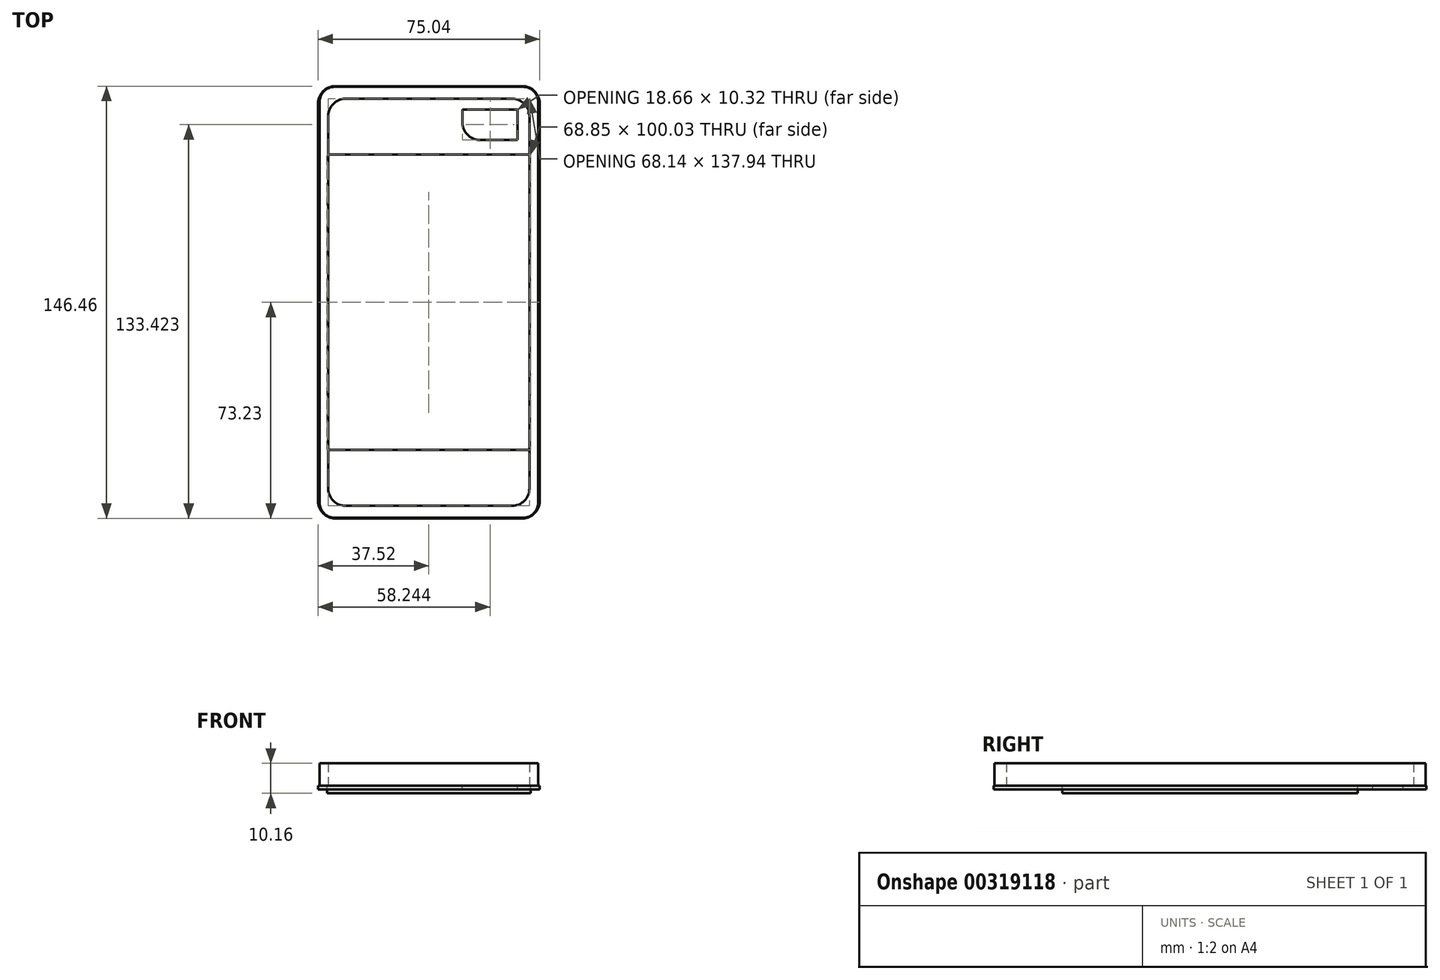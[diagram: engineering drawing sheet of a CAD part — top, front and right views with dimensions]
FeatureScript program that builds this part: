
annotation { "Feature Type Name" : "Feature", "Feature Type Description" : "" }
export const myFeature = defineFeature(function(context is Context, id is Id, definition is map)
    precondition{}
    {
        {
            var Q0;
            Q0=qCreatedBy(makeId("Top.planeOp"),FACE);
            var sketch = newSketch(context, id + "F0", { "sketchPlane" : qUnion([Q0])});
            skLineSegment(sketch, "E0.bottom", {"start": v(-31.96, 72.99) * mm, "end": v(31.96, 72.99) * mm});
            skLineSegment(sketch, "E0.top", {"start": v(-31.96, -72.99) * mm, "end": v(31.96, -72.99) * mm});
            skLineSegment(sketch, "E0.left", {"start": v(-37.04, 67.9) * mm, "end": v(-37.04, -67.9) * mm});
            skLineSegment(sketch, "E0.right", {"start": v(37.04, 67.9) * mm, "end": v(37.04, -67.9) * mm});
            skPoint(sketch, "E0.middle", {"position": v(0, 0) * mm});
            skLineSegment(sketch, "E1.bottom", {"start": v(28.23, 68.97) * mm, "end": v(-28.23, 68.97) * mm});
            skLineSegment(sketch, "E1.top", {"start": v(28.23, -68.97) * mm, "end": v(-28.23, -68.97) * mm});
            skLineSegment(sketch, "E1.left", {"start": v(34.07, 63.13) * mm, "end": v(34.07, -63.13) * mm});
            skLineSegment(sketch, "E1.right", {"start": v(-34.07, 63.13) * mm, "end": v(-34.07, -63.13) * mm});
            skPoint(sketch, "E2.visualSharp", {"position": v(34.07, 68.97) * mm});
            skArc(sketch, "E2.filletArc", {"start": v(34.07, 63.13) * mm, "mid": v(32.36, 67.26) * mm, "end": v(28.23, 68.97) * mm});
            skPoint(sketch, "E3.visualSharp", {"position": v(-34.07, 68.97) * mm});
            skArc(sketch, "E3.filletArc", {"start": v(-28.23, 68.97) * mm, "mid": v(-32.36, 67.26) * mm, "end": v(-34.07, 63.13) * mm});
            skPoint(sketch, "E4.visualSharp", {"position": v(-34.07, -68.97) * mm});
            skArc(sketch, "E4.filletArc", {"start": v(-34.07, -63.13) * mm, "mid": v(-32.36, -67.26) * mm, "end": v(-28.23, -68.97) * mm});
            skPoint(sketch, "E5.visualSharp", {"position": v(34.07, -68.97) * mm});
            skArc(sketch, "E5.filletArc", {"start": v(28.23, -68.97) * mm, "mid": v(32.36, -67.26) * mm, "end": v(34.07, -63.13) * mm});
            skPoint(sketch, "E6.visualSharp", {"position": v(37.04, 72.99) * mm});
            skArc(sketch, "E6.filletArc", {"start": v(37.04, 67.9) * mm, "mid": v(35.55, 71.5) * mm, "end": v(31.96, 72.99) * mm});
            skPoint(sketch, "E7.visualSharp", {"position": v(-37.04, 72.99) * mm});
            skArc(sketch, "E7.filletArc", {"start": v(-31.96, 72.99) * mm, "mid": v(-35.55, 71.5) * mm, "end": v(-37.04, 67.9) * mm});
            skPoint(sketch, "E8.visualSharp", {"position": v(37.04, -72.99) * mm});
            skArc(sketch, "E8.filletArc", {"start": v(31.96, -72.99) * mm, "mid": v(35.55, -71.5) * mm, "end": v(37.04, -67.9) * mm});
            skPoint(sketch, "E9.visualSharp", {"position": v(-37.04, -72.99) * mm});
            skArc(sketch, "E9.filletArc", {"start": v(-37.04, -67.9) * mm, "mid": v(-35.55, -71.5) * mm, "end": v(-31.96, -72.99) * mm});
            skSolve(sketch);
        }
        {
            var Q0;
            Q0=qCreatedBy(makeId("Top.planeOp"),FACE);
            var sketch = newSketch(context, id + "F1", { "sketchPlane" : qUnion([Q0])});
            skLineSegment(sketch, "E10.bottom", {"start": v(-31.68, -73.23) * mm, "end": v(31.68, -73.23) * mm});
            skLineSegment(sketch, "E10.top", {"start": v(-31.68, 73.23) * mm, "end": v(31.68, 73.23) * mm});
            skLineSegment(sketch, "E10.left", {"start": v(-37.52, -67.39) * mm, "end": v(-37.52, 67.39) * mm});
            skLineSegment(sketch, "E10.right", {"start": v(37.52, -67.39) * mm, "end": v(37.52, 67.39) * mm});
            skPoint(sketch, "E10.middle", {"position": v(0, 0) * mm});
            skPoint(sketch, "E11.visualSharp", {"position": v(37.52, 73.23) * mm});
            skArc(sketch, "E11.filletArc", {"start": v(37.52, 67.39) * mm, "mid": v(35.81, 71.52) * mm, "end": v(31.68, 73.23) * mm});
            skPoint(sketch, "E12.visualSharp", {"position": v(-37.52, 73.23) * mm});
            skArc(sketch, "E12.filletArc", {"start": v(-31.68, 73.23) * mm, "mid": v(-35.81, 71.52) * mm, "end": v(-37.52, 67.39) * mm});
            skPoint(sketch, "E13.visualSharp", {"position": v(-37.52, -73.23) * mm});
            skArc(sketch, "E13.filletArc", {"start": v(-37.52, -67.39) * mm, "mid": v(-35.81, -71.52) * mm, "end": v(-31.68, -73.23) * mm});
            skPoint(sketch, "E14.visualSharp", {"position": v(37.52, -73.23) * mm});
            skArc(sketch, "E14.filletArc", {"start": v(31.68, -73.23) * mm, "mid": v(35.81, -71.52) * mm, "end": v(37.52, -67.39) * mm});
            skLineSegment(sketch, "E15.bottom", {"start": v(30.05, 65.35) * mm, "end": v(11.4, 65.35) * mm});
            skLineSegment(sketch, "E15.top", {"start": v(30.05, 55.03) * mm, "end": v(17.24, 55.03) * mm});
            skLineSegment(sketch, "E15.left", {"start": v(30.05, 65.35) * mm, "end": v(30.05, 55.03) * mm});
            skLineSegment(sketch, "E15.right", {"start": v(11.4, 65.35) * mm, "end": v(11.4, 60.87) * mm});
            skPoint(sketch, "E16.visualSharp", {"position": v(11.4, 55.03) * mm});
            skArc(sketch, "E16.filletArc", {"start": v(11.4, 60.87) * mm, "mid": v(13.1, 56.74) * mm, "end": v(17.24, 55.03) * mm});
            skLineSegment(sketch, "E17.bottom", {"start": v(-34.43, -50.02) * mm, "end": v(34.43, -50.02) * mm});
            skLineSegment(sketch, "E17.top", {"start": v(-34.43, 50.02) * mm, "end": v(34.43, 50.02) * mm});
            skLineSegment(sketch, "E17.left", {"start": v(-34.43, -50.02) * mm, "end": v(-34.43, 50.02) * mm});
            skLineSegment(sketch, "E17.right", {"start": v(34.43, -50.02) * mm, "end": v(34.43, 50.02) * mm});
            skSolve(sketch);
        }
        {
            var Q0;
            Q0=makeQuery(id+"F1.imprint","IMPRINT",FACE,{"disambiguationData":[TD([[makeQuery(id+"F1.imprint","IMPRINT",EDGE,{"derivedFrom":sQuery(id+"F1.wireOp",EDGE,"E10.bottom")}),1.0]])]});
            extrude(context, id + "F2", {"entities" : qUnion([Q0]), "oppositeDirection" : true, "depth" : 1.27 * mm});
        }
        {
            var Q0;
            Q0 = qSketchRegion(id + "F0", true);
            extrude(context, id + "F3", {"entities" : qUnion([Q0]), "depth" : 7.62 * mm});
        }
        {
            var Q0;
            Q0=makeQuery(id+"F1.imprint","IMPRINT",FACE,{"disambiguationData":[TD([[makeQuery(id+"F1.imprint","IMPRINT",EDGE,{"derivedFrom":sQuery(id+"F1.wireOp",EDGE,"E17.bottom")}),1.0]])]});
            extrude(context, id + "F4", {"entities" : qUnion([Q0]), "oppositeDirection" : true, "depth" : 2.54 * mm});
        }
    });
